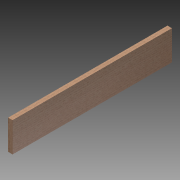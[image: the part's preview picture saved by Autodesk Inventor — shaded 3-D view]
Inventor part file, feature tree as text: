
AUTODESK INVENTOR PART (.ipt)
format: ipt  version: 2014 SP1 (Build 180222100, 222)  size: 96,256 bytes
history: native  units: in
note: dims shown in document units (in); Inventor stores cm internally (conversion verified against a paired STEP export)
features: extrude x1, sketch x1
ambient origin geometry x8: Origin, YZ Plane, XZ Plane, XY Plane, X Axis, Y Axis, Z Axis, Center Point
bodies: Solid1 (feature_tree)
feature tree (2):
  extrude  "Extrusion1"  Depth=0.75in
  sketch  "Sketch1"  dims[d0=5.0in d1=0.75in d2=26.875in d3=0.0in]
